# Revit family: Maxlogic manual call poınt resettable (High IP)
name_source: partatom
category: Fire Alarm Devices
units: mm (PartAtom-declared; Revit-internal decimal feet)

## family parameters
Cut with Voids When Loaded = No
Host = Face
Maintain Annotation Orientation = Yes
OmniClass Number = 23.85.30.21
OmniClass Title = Environmental Detection/Registration
Part Type = Normal
Room Calculation Point = No
Round Connector Dimension = Use Diameter
Shared = No

## types (5) — shared parameters
Color = Red
Device Adress Setup = The address is given to devices by addressable programmer
Fax Number = (+)90 216 466 45 10
Installation Manual = https://mavilielektronik.com
Main Material = Red Plastic PC/ABS
Manufacturer = Mavili Elektronik Ticaret A.Ş.
Mounting height = 140 cm above from ground (+/-200mm)
Mounting surface = Wall mounting
Nominal Depth = 71 mm
Nominal Height = 97,5 mm
Nominal Width = 93 mm
Operating voltage range = 18-33V/DC
Operatonal Voltage (default) = 24 V/DC
Protective Cover = PS200
Secondary Material = Plastic
URL = https://www.mavili.com.tr
Warranty Duration Labor = 2
Warranty Duration Parts = 2
Warranty Duration Unit = Year
zero-valued in all types: Cost, Default Elevation

## per-type parameters (varying)
| type | Code Performance | Description | Model | Operating temperature | Product Code | Protection Sign | Weight |
| Maxlogic Intelligent Addressable manual call point, waterproof (IP67), resettable | EN 54-11 and EN 54-17 | Intelligent Addressable manual call point, waterproof (IP67), resettable | MaxLogic | (-30°C) - (+70°C) | ML-1730 | IP67 | 270 g |
| Maxlogic Intelligent Addressable manual call point, waterproof (IP67), resettable, short circuit isolator | EN 54-11 and EN 54-17 | Intelligent Addressable manual call point, waterproof (IP67), resettable, short circuit isolator | MaxLogic | (-30°C) - (+70°C) | ML-1730.SCI | IP67 | 270 g |
| Mavigard Addressable manual call point, waterproof (IP67), resettable | EN 54-11 | Addressable manual call point, waterproof (IP67), resettable | Mavigard | (-30°C) - (+70°C) | MG-8120 | IP67 | 240 g |
| Maxlogic Intelligent Addressable System Manual Call Point, Resettable, Weatherproof (IP65) | EN 54-11 and EN 54-17 | Intelligent Addressable System Manual Call Point, Resettable, Weatherproof (IP65) | MaxLogic | (-25°C) - (+70°C) | ML-1731 | IP65 | 270 g |
| Maxlogic Intelligent Addressable System Manual Call Point, Resettable, Weatherproof (IP65) With Short Circuit Isolator | EN 54-11 and EN 54-17 | Intelligent Addressable System Manual Call Point, Resettable, Weatherproof (IP65) With Short Circuit Isolator | MaxLogic | (-25°C) - (+70°C) | ML-1731.SCI | IP65 | 270 g |

## geometry (parser evidence)
native form markers: Sweep x2
no freeform markers — native parametric forms only
